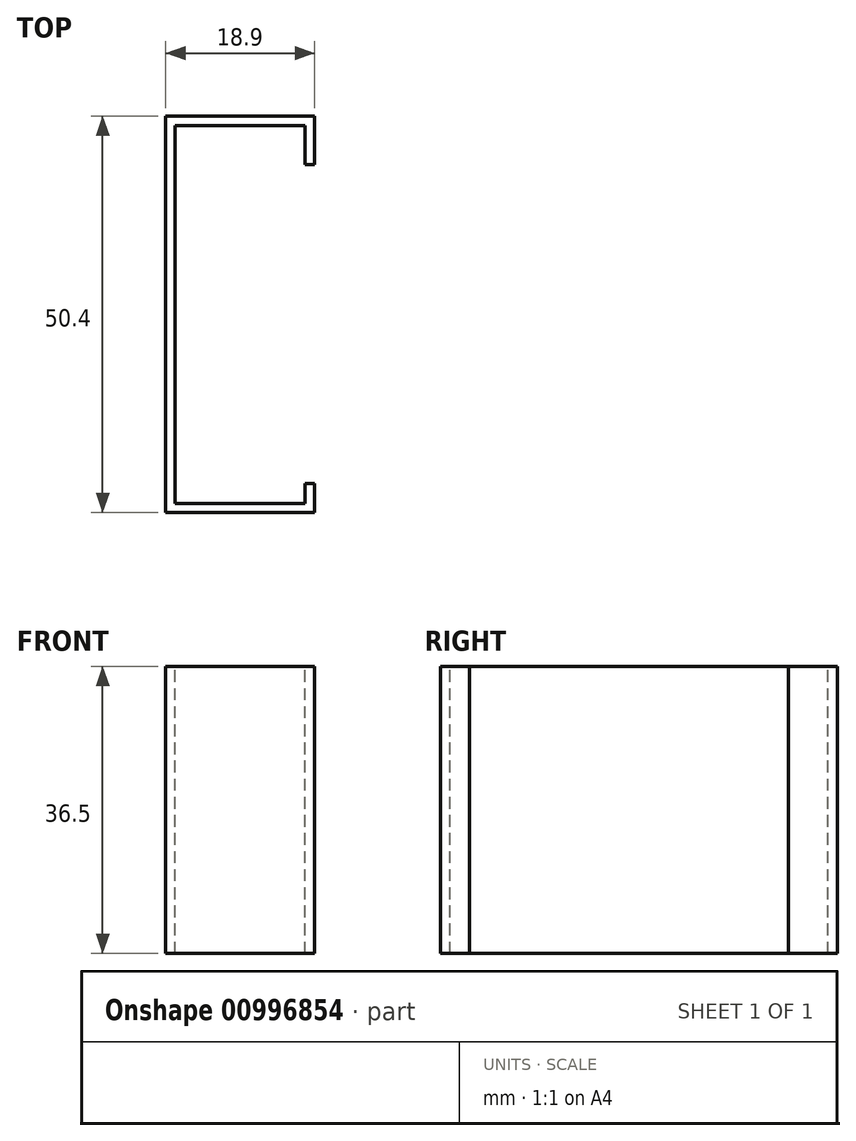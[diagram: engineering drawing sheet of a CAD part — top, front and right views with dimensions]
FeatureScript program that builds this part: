
annotation { "Feature Type Name" : "Feature", "Feature Type Description" : "" }
export const myFeature = defineFeature(function(context is Context, id is Id, definition is map)
    precondition{}
    {
        {
            var Q0;
            Q0=qCreatedBy(makeId("Top.planeOp"),FACE);
            var sketch = newSketch(context, id + "F0", { "sketchPlane" : qUnion([Q0])});
            skLineSegment(sketch, "E0", {"start": v(0, 0) * mm, "end": v(0, 48) * mm});
            skLineSegment(sketch, "E1", {"start": v(0, 48) * mm, "end": v(16.5, 48) * mm});
            skLineSegment(sketch, "E2", {"start": v(0, 0) * mm, "end": v(16.5, 0) * mm});
            skLineSegment(sketch, "E3", {"start": v(16.5, 0) * mm, "end": v(16.5, 2.5) * mm});
            skLineSegment(sketch, "E4", {"start": v(16.5, 48) * mm, "end": v(16.5, 43) * mm});
            skLineSegment(sketch, "E5", {"start": v(16.5, 43) * mm, "end": v(17.7, 43) * mm});
            skLineSegment(sketch, "E6", {"start": v(17.7, 43) * mm, "end": v(17.7, 49.2) * mm});
            skLineSegment(sketch, "E7", {"start": v(17.7, 49.2) * mm, "end": v(-1.2, 49.2) * mm});
            skLineSegment(sketch, "E8", {"start": v(-1.2, 49.2) * mm, "end": v(-1.2, -1.2) * mm});
            skLineSegment(sketch, "E9", {"start": v(-1.2, -1.2) * mm, "end": v(17.7, -1.2) * mm});
            skLineSegment(sketch, "E10", {"start": v(17.7, -1.2) * mm, "end": v(17.7, 2.5) * mm});
            skLineSegment(sketch, "E11", {"start": v(17.7, 2.5) * mm, "end": v(16.5, 2.5) * mm});
            skSolve(sketch);
        }
        {
            var Q0;
            Q0=makeQuery(id+"F0.imprint","IMPRINT",FACE,{"disambiguationData":[TD([[makeQuery(id+"F0.imprint","IMPRINT",EDGE,{"derivedFrom":sQuery(id+"F0.wireOp",EDGE,"E0")}),1.0]])]});
            extrude(context, id + "F1", {"entities" : qUnion([Q0]), "oppositeDirection" : true, "depth" : 36.5 * mm, "offsetDistance" : 25 * mm});
        }
    });
